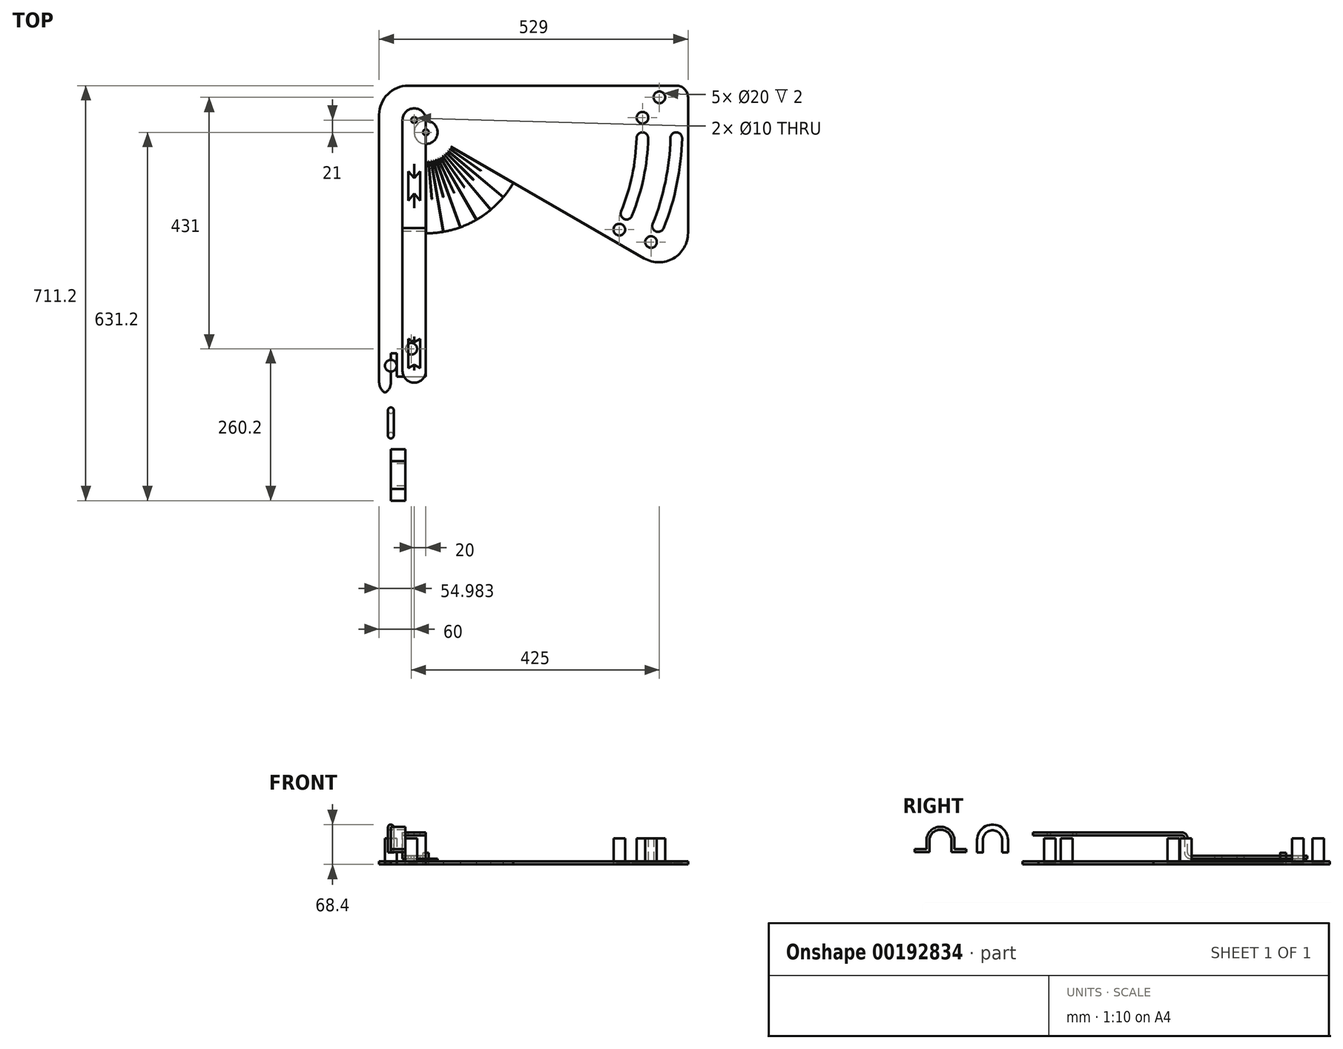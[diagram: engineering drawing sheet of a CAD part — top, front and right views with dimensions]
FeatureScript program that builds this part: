
annotation { "Feature Type Name" : "Feature", "Feature Type Description" : "" }
export const myFeature = defineFeature(function(context is Context, id is Id, definition is map)
    precondition{}
    {
        {
            var Q0;
            Q0=qCreatedBy(makeId("Top.planeOp"),FACE);
            var sketch = newSketch(context, id + "F0", { "sketchPlane" : qUnion([Q0])});
            skLineSegment(sketch, "E0.bottom", {"start": v(0, 0) * mm, "end": v(489, 0) * mm});
            skLineSegment(sketch, "E0.left", {"start": v(0, 0) * mm, "end": v(0, 500) * mm});
            skLineSegment(sketch, "E0.right", {"start": v(489, 0) * mm, "end": v(489, 479) * mm});
            skLineSegment(sketch, "E1.top", {"start": v(0, 0) * mm, "end": v(10, 0) * mm});
            skLineSegment(sketch, "E1.left", {"start": v(0, 489) * mm, "end": v(0, 0) * mm});
            skLineSegment(sketch, "E1.right", {"start": v(10, 50) * mm, "end": v(10, 10) * mm});
            skPoint(sketch, "E2", {"position": v(60, 429) * mm});
            skLineSegment(sketch, "E3", {"start": v(60, 255.9) * mm, "end": v(60, 0) * mm});
            skLineSegment(sketch, "E4", {"start": v(209.9, 342.45) * mm, "end": v(489, 181.32) * mm});
            skLineSegment(sketch, "E5.bottom", {"start": v(10, 48) * mm, "end": v(60, 48) * mm, "construction": true});
            skLineSegment(sketch, "E5.right", {"start": v(60, 48) * mm, "end": v(60, 10) * mm, "construction": true});
            skLineSegment(sketch, "E6.top", {"start": v(441, 429) * mm, "end": v(479, 429) * mm, "construction": true});
            skLineSegment(sketch, "E6.left", {"start": v(441, 479) * mm, "end": v(441, 429) * mm, "construction": true});
            skArc(sketch, "E7", {"start": v(60, 29) * mm, "mid": v(342.84, 146.16) * mm, "end": v(460, 429) * mm, "construction": true});
            skPoint(sketch, "E8", {"position": v(10, 29) * mm});
            skPoint(sketch, "E9", {"position": v(460, 479) * mm});
            skArc(sketch, "E10.0", {"start": v(60, 10) * mm, "mid": v(356.28, 132.72) * mm, "end": v(479, 429) * mm, "construction": true});
            skArc(sketch, "E11.0", {"start": v(60, 48) * mm, "mid": v(329.4, 159.6) * mm, "end": v(441, 429) * mm, "construction": true});
            skLineSegment(sketch, "E12", {"start": v(60, 255.9) * mm, "end": v(209.9, 342.45) * mm, "construction": true});
            skPoint(sketch, "E13.end.orphan", {"position": v(189.9, 354) * mm});
            skPoint(sketch, "E13.start.orphan", {"position": v(60, 279) * mm});
            skCircle(sketch, "E14", {"center": v(60, 429) * mm, "radius": 5 * mm});
            skLineSegment(sketch, "E15.top", {"start": v(489, 489) * mm, "end": v(0, 489) * mm});
            skLineSegment(sketch, "E15.left", {"start": v(489, 479) * mm, "end": v(489, 489) * mm});
            skLineSegment(sketch, "E16", {"start": v(439, 489) * mm, "end": v(439, 479) * mm});
            skLineSegment(sketch, "E17", {"start": v(439, 479) * mm, "end": v(479, 479) * mm});
            skLineSegment(sketch, "E18", {"start": v(479, 479) * mm, "end": v(479, 429) * mm});
            skLineSegment(sketch, "E19", {"start": v(489, 429) * mm, "end": v(479, 429) * mm});
            skArc(sketch, "E20", {"start": v(60, 255.9) * mm, "mid": v(146.55, 279.1) * mm, "end": v(209.9, 342.45) * mm});
            skLineSegment(sketch, "E21", {"start": v(0, 50) * mm, "end": v(10, 50) * mm});
            skLineSegment(sketch, "E22", {"start": v(10, 10) * mm, "end": v(60, 10) * mm});
            skLineSegment(sketch, "E23", {"start": v(60, 0) * mm, "end": v(60, -20) * mm});
            skLineSegment(sketch, "E24", {"start": v(60, -20) * mm, "end": v(0, -20) * mm});
            skLineSegment(sketch, "E25", {"start": v(0, -20) * mm, "end": v(0, 0) * mm});
            skLineSegment(sketch, "E26", {"start": v(0, 489) * mm, "end": v(-20, 489) * mm});
            skLineSegment(sketch, "E27", {"start": v(-20, 489) * mm, "end": v(-20, -20) * mm});
            skLineSegment(sketch, "E28", {"start": v(-20, -20) * mm, "end": v(0, -20) * mm});
            skLineSegment(sketch, "E29", {"start": v(489, 181.32) * mm, "end": v(509, 169.77) * mm});
            skLineSegment(sketch, "E30", {"start": v(509, 169.77) * mm, "end": v(509, 489) * mm});
            skLineSegment(sketch, "E31", {"start": v(509, 489) * mm, "end": v(489, 489) * mm});
            skLineSegment(sketch, "E32", {"start": v(509, 489) * mm, "end": v(509, 509) * mm});
            skLineSegment(sketch, "E33", {"start": v(509, 509) * mm, "end": v(-20, 509) * mm});
            skLineSegment(sketch, "E34", {"start": v(-20, 509) * mm, "end": v(-20, 489) * mm});
            skSolve(sketch);
        }
        {
            var Q0;
            {var subQ3=sQuery(id+"F0.wireOp",EDGE,"E1.right");Q0=makeQuery(id+"F0.imprint","IMPRINT",FACE,{"disambiguationData":[TD([[makeQuery(id+"F0.imprint","IMPRINT",EDGE,{"derivedFrom":subQ3}),1.0]])]});}
            var Q1;
            {var subQ2=sQuery(id+"F0.wireOp",EDGE,"E1.top");Q1=makeQuery(id+"F0.imprint","IMPRINT",FACE,{"disambiguationData":[TD([[makeQuery(id+"F0.imprint","IMPRINT",EDGE,{"derivedFrom":subQ2}),1.0]])]});}
            var Q2;
            {var subQ1=sQuery(id+"F0.wireOp",EDGE,"E15.left");Q2=makeQuery(id+"F0.imprint","IMPRINT",FACE,{"disambiguationData":[TD([[makeQuery(id+"F0.imprint","IMPRINT",EDGE,{"derivedFrom":subQ1}),1.0]])]});}
            var Q3;
            {var subQ1=sQuery(id+"F0.wireOp",EDGE,"E25");Q3=makeQuery(id+"F0.imprint","IMPRINT",FACE,{"disambiguationData":[TD([[makeQuery(id+"F0.imprint","IMPRINT",EDGE,{"derivedFrom":subQ1}),1.0]])]});}
            var Q4;
            {var subQ0=sQuery(id+"F0.wireOp",EDGE,"E1.top");Q4=makeQuery(id+"F0.imprint","IMPRINT",FACE,{"disambiguationData":[TD([[makeQuery(id+"F0.imprint","IMPRINT",EDGE,{"derivedFrom":subQ0}),-1.0]])]});}
            var Q5;
            {var subQ3=sQuery(id+"F0.wireOp",EDGE,"E26");Q5=makeQuery(id+"F0.imprint","IMPRINT",FACE,{"disambiguationData":[TD([[makeQuery(id+"F0.imprint","IMPRINT",EDGE,{"derivedFrom":subQ3}),-1.0]])]});}
            var Q6;
            {var subQ1=sQuery(id+"F0.wireOp",EDGE,"E15.left");Q6=makeQuery(id+"F0.imprint","IMPRINT",FACE,{"disambiguationData":[TD([[makeQuery(id+"F0.imprint","IMPRINT",EDGE,{"derivedFrom":subQ1}),-1.0]])]});}
            extrude(context, id + "F1", {"entities" : qUnion([Q0, Q1, Q2, Q3, Q4, Q5, Q6]), "depth" : 5 * mm});
        }
        {
            var Q0;
            Q0=makeQuery(id+"F1.opExtrude","SWEPT_FACE",FACE,{"disambiguationData":[OSD([sQuery(id+"F0.wireOp",EDGE,"E33")])]});
            cPlane(context, id + "F2", {"entities" : qUnion([Q0]), "cplaneType" : CPlaneType.OFFSET, "offset" : 80 * mm, "oppositeDirection" : true, "width" : 150 * mm, "height" : 150 * mm});
        }
        {
            var Q0;
            Q0=qCreatedBy(id+"F2.planeOp",FACE);
            var sketch = newSketch(context, id + "F3", { "sketchPlane" : qUnion([Q0])});
            skLineSegment(sketch, "E35", {"start": v(-60, 20) * mm, "end": v(-60, 0) * mm});
            skLineSegment(sketch, "E36", {"start": v(-60, 20) * mm, "end": v(-65, 20) * mm});
            skLineSegment(sketch, "E37", {"start": v(-65, 20) * mm, "end": v(-65, 10) * mm});
            skLineSegment(sketch, "E38", {"start": v(-65, 10) * mm, "end": v(-80, 10) * mm});
            skLineSegment(sketch, "E39", {"start": v(-80, 10) * mm, "end": v(-80, 5) * mm});
            skLineSegment(sketch, "E40", {"start": v(-80, 5) * mm, "end": v(-65, 5) * mm});
            skLineSegment(sketch, "E41", {"start": v(-65, 5) * mm, "end": v(-65, 0) * mm});
            skLineSegment(sketch, "E42", {"start": v(-65, 0) * mm, "end": v(-60, 0) * mm});
            skSolve(sketch);
        }
        {
            var Q0;
            Q0=qSketchRegion(id+"F3",true);
            var Q1;
            Q1=sQuery(id+"F3.wireOp",EDGE,"E35");
            revolve(context, id + "F4", {"entities" : qUnion([Q0]), "axis" : qUnion([Q1]), "revolveType" : RevolveType.FULL});
        }
        {
            var Q0;
            Q0=makeQuery(id+"F1.opExtrude","CAP_FACE",FACE,{"disambiguationData":[OSD([sQuery(id+"F0.wireOp",EDGE,"E0.bottom"),sQuery(id+"F0.wireOp",EDGE,"E0.top"),sQuery(id+"F0.wireOp",EDGE,"E0.right"),sQuery(id+"F0.wireOp",EDGE,"E1.right"),sQuery(id+"F0.wireOp",EDGE,"E3"),sQuery(id+"F0.wireOp",EDGE,"E4"),sQuery(id+"F0.wireOp",EDGE,"E12"),sQuery(id+"F0.wireOp",EDGE,"E14")])],"isStart":false});
            cPlane(context, id + "F5", {"entities" : qUnion([Q0]), "cplaneType" : CPlaneType.OFFSET, "offset" : 0 * mm, "width" : 150 * mm, "height" : 150 * mm});
        }
        {
            var Q0;
            Q0=qCreatedBy(id+"F5.planeOp",FACE);
            var sketch = newSketch(context, id + "F6", { "sketchPlane" : qUnion([Q0])});
            skCircle(sketch, "E43", {"center": v(34.98, 58) * mm, "radius": 10 * mm});
            skLineSegment(sketch, "E44.bottom", {"start": v(9.98, 10) * mm, "end": v(59.98, 10) * mm, "construction": true});
            skLineSegment(sketch, "E44.top", {"start": v(9.98, 48) * mm, "end": v(59.98, 48) * mm, "construction": true});
            skLineSegment(sketch, "E44.left", {"start": v(9.98, 10) * mm, "end": v(9.98, 48) * mm, "construction": true});
            skLineSegment(sketch, "E44.right", {"start": v(59.98, 10) * mm, "end": v(59.98, 48) * mm, "construction": true});
            skLineSegment(sketch, "E45.bottom", {"start": v(478.98, 479) * mm, "end": v(440.98, 479) * mm, "construction": true});
            skLineSegment(sketch, "E45.top", {"start": v(478.98, 429) * mm, "end": v(440.98, 429) * mm, "construction": true});
            skLineSegment(sketch, "E45.left", {"start": v(478.98, 479) * mm, "end": v(478.98, 429) * mm, "construction": true});
            skLineSegment(sketch, "E45.right", {"start": v(440.98, 479) * mm, "end": v(440.98, 429) * mm, "construction": true});
            skArc(sketch, "E46", {"start": v(59.98, 29) * mm, "mid": v(342.83, 146.16) * mm, "end": v(459.98, 429) * mm, "construction": true});
            skArc(sketch, "E47.0", {"start": v(59.98, 10) * mm, "mid": v(356.26, 132.72) * mm, "end": v(478.98, 429) * mm, "construction": true});
            skArc(sketch, "E48.0", {"start": v(59.98, 48) * mm, "mid": v(329.4, 159.6) * mm, "end": v(440.98, 429) * mm, "construction": true});
            skLineSegment(sketch, "E49", {"start": v(459.98, 429) * mm, "end": v(459.98, 479) * mm, "construction": true});
            skLineSegment(sketch, "E50", {"start": v(59.98, 29) * mm, "end": v(9.98, 29) * mm, "construction": true});
            skCircle(sketch, "E51", {"center": v(430.98, 454) * mm, "radius": 10 * mm});
            skCircle(sketch, "E52", {"center": v(445.6, 241.01) * mm, "radius": 10 * mm});
            skLineSegment(sketch, "E53", {"start": v(445.6, 241.01) * mm, "end": v(391.37, 262.2) * mm, "construction": true});
            skCircle(sketch, "E54", {"center": v(391.37, 262.2) * mm, "radius": 10 * mm});
            skCircle(sketch, "E55.MirrorC", {"center": v(34.98, 0) * mm, "radius": 10 * mm});
            skCircle(sketch, "E56", {"center": v(-0.02, 29) * mm, "radius": 10 * mm});
            skLineSegment(sketch, "E57", {"start": v(34.98, 0) * mm, "end": v(34.98, 48) * mm, "construction": true});
            skCircle(sketch, "E58.MirrorC", {"center": v(488.98, 454) * mm, "radius": 10 * mm});
            skLineSegment(sketch, "E59", {"start": v(430.98, 454) * mm, "end": v(488.98, 454) * mm, "construction": true});
            skCircle(sketch, "E60", {"center": v(459.98, 489) * mm, "radius": 10 * mm});
            skSolve(sketch);
        }
        {
            var Q0;
            Q0=makeQuery(id+"F6.imprint","IMPRINT",FACE,{"disambiguationData":[TD([[makeQuery(id+"F6.imprint","IMPRINT",EDGE,{"derivedFrom":sQuery(id+"F6.wireOp",EDGE,"E58.MirrorC")}),-1.0]])]});
            var Q1;
            Q1=makeQuery(id+"F6.imprint","IMPRINT",FACE,{"disambiguationData":[TD([[makeQuery(id+"F6.imprint","IMPRINT",EDGE,{"derivedFrom":sQuery(id+"F6.wireOp",EDGE,"E60")}),1.0]])]});
            var Q2;
            Q2=makeQuery(id+"F6.imprint","IMPRINT",FACE,{"disambiguationData":[TD([[makeQuery(id+"F6.imprint","IMPRINT",EDGE,{"derivedFrom":sQuery(id+"F6.wireOp",EDGE,"E51")}),1.0]])]});
            var Q3;
            Q3=makeQuery(id+"F6.imprint","IMPRINT",FACE,{"disambiguationData":[TD([[makeQuery(id+"F6.imprint","IMPRINT",EDGE,{"derivedFrom":sQuery(id+"F6.wireOp",EDGE,"E52")}),1.0]])]});
            var Q4;
            Q4=makeQuery(id+"F6.imprint","IMPRINT",FACE,{"disambiguationData":[TD([[makeQuery(id+"F6.imprint","IMPRINT",EDGE,{"derivedFrom":sQuery(id+"F6.wireOp",EDGE,"E54")}),1.0]])]});
            var Q5;
            Q5=makeQuery(id+"F6.imprint","IMPRINT",FACE,{"disambiguationData":[TD([[makeQuery(id+"F6.imprint","IMPRINT",EDGE,{"derivedFrom":sQuery(id+"F6.wireOp",EDGE,"E55.MirrorC")}),-1.0]])]});
            var Q6;
            Q6=makeQuery(id+"F6.imprint","IMPRINT",FACE,{"disambiguationData":[TD([[makeQuery(id+"F6.imprint","IMPRINT",EDGE,{"derivedFrom":sQuery(id+"F6.wireOp",EDGE,"E43")}),1.0]])]});
            var Q7;
            Q7=makeQuery(id+"F6.imprint","IMPRINT",FACE,{"disambiguationData":[TD([[makeQuery(id+"F6.imprint","IMPRINT",EDGE,{"derivedFrom":sQuery(id+"F6.wireOp",EDGE,"E56")}),1.0]])]});
            extrude(context, id + "F7", {"entities" : qUnion([Q0, Q1, Q2, Q3, Q4, Q5, Q6, Q7]), "operationType" : NewBodyOperationType.REMOVE, "oppositeDirection" : true, "depth" : 2 * mm});
        }
        {
            var Q0;
            Q0=makeQuery(id+"F6.imprint","IMPRINT",FACE,{"disambiguationData":[TD([[makeQuery(id+"F6.imprint","IMPRINT",EDGE,{"derivedFrom":sQuery(id+"F6.wireOp",EDGE,"E58.MirrorC")}),-1.0]])]});
            var Q1;
            Q1=makeQuery(id+"F6.imprint","IMPRINT",FACE,{"disambiguationData":[TD([[makeQuery(id+"F6.imprint","IMPRINT",EDGE,{"derivedFrom":sQuery(id+"F6.wireOp",EDGE,"E60")}),1.0]])]});
            var Q2;
            Q2=makeQuery(id+"F6.imprint","IMPRINT",FACE,{"disambiguationData":[TD([[makeQuery(id+"F6.imprint","IMPRINT",EDGE,{"derivedFrom":sQuery(id+"F6.wireOp",EDGE,"E51")}),1.0]])]});
            var Q3;
            Q3=makeQuery(id+"F6.imprint","IMPRINT",FACE,{"disambiguationData":[TD([[makeQuery(id+"F6.imprint","IMPRINT",EDGE,{"derivedFrom":sQuery(id+"F6.wireOp",EDGE,"E52")}),1.0]])]});
            var Q4;
            Q4=makeQuery(id+"F6.imprint","IMPRINT",FACE,{"disambiguationData":[TD([[makeQuery(id+"F6.imprint","IMPRINT",EDGE,{"derivedFrom":sQuery(id+"F6.wireOp",EDGE,"E54")}),1.0]])]});
            var Q5;
            Q5=makeQuery(id+"F6.imprint","IMPRINT",FACE,{"disambiguationData":[TD([[makeQuery(id+"F6.imprint","IMPRINT",EDGE,{"derivedFrom":sQuery(id+"F6.wireOp",EDGE,"E56")}),1.0]])]});
            var Q6;
            Q6=makeQuery(id+"F6.imprint","IMPRINT",FACE,{"disambiguationData":[TD([[makeQuery(id+"F6.imprint","IMPRINT",EDGE,{"derivedFrom":sQuery(id+"F6.wireOp",EDGE,"E55.MirrorC")}),-1.0]])]});
            var Q7;
            Q7=makeQuery(id+"F6.imprint","IMPRINT",FACE,{"disambiguationData":[TD([[makeQuery(id+"F6.imprint","IMPRINT",EDGE,{"derivedFrom":sQuery(id+"F6.wireOp",EDGE,"E43")}),1.0]])]});
            extrude(context, id + "F8", {"entities" : qUnion([Q0, Q1, Q2, Q3, Q4, Q5, Q6, Q7]), "depth" : 40 * mm});
        }
        {
            var Q0;
            Q0=makeQuery(id+"F1.opExtrude","CAP_FACE",FACE,{"disambiguationData":[OSD([sQuery(id+"F0.wireOp",EDGE,"E0.bottom"),sQuery(id+"F0.wireOp",EDGE,"E0.right"),sQuery(id+"F0.wireOp",EDGE,"E1.right"),sQuery(id+"F0.wireOp",EDGE,"E3"),sQuery(id+"F0.wireOp",EDGE,"E4"),sQuery(id+"F0.wireOp",EDGE,"E12"),sQuery(id+"F0.wireOp",EDGE,"E14"),sQuery(id+"F0.wireOp",EDGE,"E15.top"),sQuery(id+"F0.wireOp",EDGE,"E16"),sQuery(id+"F0.wireOp",EDGE,"E17"),sQuery(id+"F0.wireOp",EDGE,"E18"),sQuery(id+"F0.wireOp",EDGE,"E19")])],"isStart":false});
            var sketch = newSketch(context, id + "F9", { "sketchPlane" : qUnion([Q0])});
            skLineSegment(sketch, "E61", {"start": v(60, 379) * mm, "end": v(60, 255.9) * mm});
            skLineSegment(sketch, "E62", {"start": v(103.3, 404) * mm, "end": v(209.9, 342.45) * mm});
            skArc(sketch, "E63", {"start": v(60, 314) * mm, "mid": v(117.5, 329.4) * mm, "end": v(159.6, 371.5) * mm});
            skLineSegment(sketch, "E64.0", {"start": v(64.45, 426.72) * mm, "end": v(210.03, 342.67) * mm});
            skArc(sketch, "E65", {"start": v(60, 424) * mm, "mid": v(62.6, 424.73) * mm, "end": v(64.45, 426.72) * mm});
            skLineSegment(sketch, "E66.trimOffspring", {"start": v(64.2, 426.29) * mm, "end": v(64.83, 425.92) * mm});
            skLineSegment(sketch, "E67", {"start": v(210.03, 342.67) * mm, "end": v(209.9, 342.45) * mm});
            skLineSegment(sketch, "E68", {"start": v(100.96, 400.32) * mm, "end": v(154.2, 363.04) * mm});
            skLineSegment(sketch, "E69", {"start": v(98.3, 396.86) * mm, "end": v(192.6, 317.74) * mm});
            skLineSegment(sketch, "E70", {"start": v(95.36, 393.64) * mm, "end": v(141.32, 347.68) * mm});
            skLineSegment(sketch, "E71", {"start": v(92.14, 390.7) * mm, "end": v(171.26, 296.4) * mm});
            skLineSegment(sketch, "E72", {"start": v(88.68, 388.04) * mm, "end": v(125.96, 334.8) * mm});
            skLineSegment(sketch, "E73", {"start": v(85, 385.7) * mm, "end": v(146.55, 279.1) * mm});
            skLineSegment(sketch, "E74", {"start": v(81.13, 383.68) * mm, "end": v(108.6, 324.77) * mm});
            skLineSegment(sketch, "E75", {"start": v(77.1, 382.02) * mm, "end": v(119.2, 266.34) * mm});
            skLineSegment(sketch, "E76", {"start": v(72.94, 380.7) * mm, "end": v(89.76, 317.92) * mm});
            skLineSegment(sketch, "E77", {"start": v(68.68, 379.76) * mm, "end": v(90.06, 258.54) * mm});
            skLineSegment(sketch, "E78", {"start": v(64.36, 379.2) * mm, "end": v(70.02, 314.44) * mm});
            skArc(sketch, "E79", {"start": v(60, 255.9) * mm, "mid": v(146.55, 279.1) * mm, "end": v(209.9, 342.45) * mm, "construction": true});
            skPoint(sketch, "E80.orphan", {"position": v(117.5, 329.4) * mm});
            skLineSegment(sketch, "E81.0", {"start": v(64.24, 426.34) * mm, "end": v(64.83, 425.92) * mm});
            skLineSegment(sketch, "E82.0", {"start": v(63.95, 425.93) * mm, "end": v(64.55, 425.51) * mm});
            skLineSegment(sketch, "E83.0", {"start": v(63.67, 425.6) * mm, "end": v(64.23, 425.13) * mm});
            skLineSegment(sketch, "E84.0", {"start": v(64, 425.98) * mm, "end": v(64.55, 425.51) * mm});
            skLineSegment(sketch, "E85.0", {"start": v(63.36, 425.29) * mm, "end": v(63.87, 424.77) * mm});
            skLineSegment(sketch, "E86.0", {"start": v(63.71, 425.64) * mm, "end": v(64.23, 425.13) * mm});
            skLineSegment(sketch, "E87.0", {"start": v(63.02, 425) * mm, "end": v(63.49, 424.45) * mm});
            skLineSegment(sketch, "E88.0", {"start": v(63.4, 425.33) * mm, "end": v(63.87, 424.77) * mm});
            skLineSegment(sketch, "E89.0", {"start": v(63.07, 425.05) * mm, "end": v(63.49, 424.45) * mm});
            skLineSegment(sketch, "E90.0", {"start": v(62.66, 424.76) * mm, "end": v(63.08, 424.17) * mm});
            skLineSegment(sketch, "E91.0", {"start": v(55.7, 435.96) * mm, "end": v(62.65, 423.92) * mm});
            skLineSegment(sketch, "E92.0", {"start": v(56.12, 436.21) * mm, "end": v(63.08, 424.17) * mm});
            skLineSegment(sketch, "E93.0", {"start": v(61.89, 424.36) * mm, "end": v(62.2, 423.7) * mm});
            skLineSegment(sketch, "E94.0", {"start": v(62.34, 424.57) * mm, "end": v(62.65, 423.92) * mm});
            skLineSegment(sketch, "E95.0", {"start": v(61.48, 424.22) * mm, "end": v(61.72, 423.53) * mm});
            skLineSegment(sketch, "E96.0", {"start": v(61.95, 424.39) * mm, "end": v(62.2, 423.7) * mm});
            skLineSegment(sketch, "E97.0", {"start": v(61.05, 424.1) * mm, "end": v(61.24, 423.4) * mm});
            skLineSegment(sketch, "E98.0", {"start": v(61.54, 424.24) * mm, "end": v(61.72, 423.53) * mm});
            skLineSegment(sketch, "E99.0", {"start": v(60.62, 424.03) * mm, "end": v(60.75, 423.32) * mm});
            skLineSegment(sketch, "E100.0", {"start": v(61.11, 424.12) * mm, "end": v(61.24, 423.4) * mm});
            skLineSegment(sketch, "E101.0", {"start": v(60.19, 424) * mm, "end": v(60.25, 423.27) * mm});
            skLineSegment(sketch, "E102.0", {"start": v(60.68, 424.04) * mm, "end": v(60.75, 423.32) * mm});
            skLineSegment(sketch, "E103.0", {"start": v(59.75, 429) * mm, "end": v(59.75, 255.9) * mm});
            skLineSegment(sketch, "E104.0", {"start": v(60.25, 424) * mm, "end": v(60.25, 423.27) * mm});
            skArc(sketch, "E105", {"start": v(103.3, 404) * mm, "mid": v(85, 385.7) * mm, "end": v(60, 379) * mm});
            skLineSegment(sketch, "E106.trimOffspring", {"start": v(60.25, 379) * mm, "end": v(60.25, 255.9) * mm});
            skLineSegment(sketch, "E107.trimOffspring", {"start": v(64.1, 379.17) * mm, "end": v(69.77, 314.42) * mm});
            skLineSegment(sketch, "E108.trimOffspring", {"start": v(64.6, 379.21) * mm, "end": v(70.27, 314.46) * mm});
            skLineSegment(sketch, "E109.trimOffspring", {"start": v(68.44, 379.72) * mm, "end": v(89.81, 258.5) * mm});
            skLineSegment(sketch, "E110.trimOffspring", {"start": v(68.93, 379.8) * mm, "end": v(90.3, 258.58) * mm});
            skLineSegment(sketch, "E111.trimOffspring", {"start": v(72.7, 380.64) * mm, "end": v(89.52, 317.85) * mm});
            skLineSegment(sketch, "E112.trimOffspring", {"start": v(73.18, 380.77) * mm, "end": v(90, 317.98) * mm});
            skLineSegment(sketch, "E113.trimOffspring", {"start": v(76.87, 381.93) * mm, "end": v(118.97, 266.26) * mm});
            skLineSegment(sketch, "E114.trimOffspring", {"start": v(77.34, 382.1) * mm, "end": v(119.44, 266.43) * mm});
            skLineSegment(sketch, "E115.trimOffspring", {"start": v(80.9, 383.58) * mm, "end": v(108.37, 324.67) * mm});
            skLineSegment(sketch, "E116.trimOffspring", {"start": v(81.36, 383.8) * mm, "end": v(108.83, 324.88) * mm});
            skLineSegment(sketch, "E117.trimOffspring", {"start": v(88.47, 387.9) * mm, "end": v(125.76, 334.65) * mm});
            skLineSegment(sketch, "E118.trimOffspring", {"start": v(88.88, 388.19) * mm, "end": v(126.17, 334.94) * mm});
            skLineSegment(sketch, "E119.trimOffspring", {"start": v(84.78, 385.57) * mm, "end": v(146.33, 278.97) * mm});
            skLineSegment(sketch, "E120.trimOffspring", {"start": v(85.22, 385.82) * mm, "end": v(146.76, 279.22) * mm});
            skLineSegment(sketch, "E121.trimOffspring", {"start": v(91.95, 390.54) * mm, "end": v(171.07, 296.24) * mm});
            skLineSegment(sketch, "E122.trimOffspring", {"start": v(92.33, 390.86) * mm, "end": v(171.45, 296.56) * mm});
            skLineSegment(sketch, "E123.trimOffspring", {"start": v(95.18, 393.47) * mm, "end": v(141.14, 347.5) * mm});
            skLineSegment(sketch, "E124.trimOffspring", {"start": v(95.53, 393.82) * mm, "end": v(141.5, 347.86) * mm});
            skLineSegment(sketch, "E125.trimOffspring", {"start": v(98.14, 396.67) * mm, "end": v(192.44, 317.55) * mm});
            skLineSegment(sketch, "E126.trimOffspring", {"start": v(98.46, 397.05) * mm, "end": v(192.76, 317.93) * mm});
            skLineSegment(sketch, "E127.trimOffspring", {"start": v(100.81, 400.12) * mm, "end": v(154.06, 362.83) * mm});
            skLineSegment(sketch, "E128.trimOffspring", {"start": v(101.1, 400.53) * mm, "end": v(154.35, 363.24) * mm});
            skLineSegment(sketch, "E129.trimOffspring", {"start": v(103.18, 403.78) * mm, "end": v(209.78, 342.24) * mm});
            skArc(sketch, "E130", {"start": v(209.9, 342.45) * mm, "mid": v(146.55, 279.1) * mm, "end": v(60, 255.9) * mm});
            skSolve(sketch);
        }
        {
            var Q0;
            {var subQ0=sQuery(id+"F9.wireOp",EDGE,"E105");var subQ1=sQuery(id+"F9.wireOp",EDGE,"E62");var subQ2=makeQuery(id+"F9.imprint","INTERSECT",VERTEX,{"derivedFrom":[subQ1,subQ0]});Q0=makeQuery(id+"F9.imprint","IMPRINT",FACE,{"disambiguationData":[TD([[makeQuery(id+"F9.imprint","IMPRINT",EDGE,{"disambiguationData":[TD([[subQ2,-1.0]])],"derivedFrom":subQ1}),-1.0]])]});}
            var Q1;
            {var subQ0=sQuery(id+"F9.wireOp",EDGE,"E62");var subQ3=sQuery(id+"F9.wireOp",EDGE,"E63");var subQ4=makeQuery(id+"F9.imprint","INTERSECT",VERTEX,{"derivedFrom":[subQ0,subQ3]});Q1=makeQuery(id+"F9.imprint","IMPRINT",FACE,{"disambiguationData":[TD([[makeQuery(id+"F9.imprint","IMPRINT",EDGE,{"disambiguationData":[TD([[subQ4,1.0]])],"derivedFrom":subQ3}),-1.0]])]});}
            var Q2;
            {var subQ0=sQuery(id+"F9.wireOp",EDGE,"E68");Q2=makeQuery(id+"F9.imprint","IMPRINT",FACE,{"disambiguationData":[TD([[makeQuery(id+"F9.imprint","IMPRINT",EDGE,{"derivedFrom":subQ0}),1.0]])]});}
            var Q3;
            {var subQ0=sQuery(id+"F9.wireOp",EDGE,"E68");Q3=makeQuery(id+"F9.imprint","IMPRINT",FACE,{"disambiguationData":[TD([[makeQuery(id+"F9.imprint","IMPRINT",EDGE,{"derivedFrom":subQ0}),-1.0]])]});}
            var Q4;
            {var subQ0=sQuery(id+"F9.wireOp",EDGE,"E69");var subQ1=sQuery(id+"F9.wireOp",EDGE,"E63");var subQ2=makeQuery(id+"F9.imprint","INTERSECT",VERTEX,{"derivedFrom":[subQ1,subQ0]});Q4=makeQuery(id+"F9.imprint","IMPRINT",FACE,{"disambiguationData":[TD([[makeQuery(id+"F9.imprint","IMPRINT",EDGE,{"disambiguationData":[TD([[subQ2,-1.0]])],"derivedFrom":subQ1}),1.0]])]});}
            var Q5;
            {var subQ0=sQuery(id+"F9.wireOp",EDGE,"E125.trimOffspring");var subQ1=sQuery(id+"F9.wireOp",EDGE,"E63");var subQ2=makeQuery(id+"F9.imprint","INTERSECT",VERTEX,{"derivedFrom":[subQ1,subQ0]});Q5=makeQuery(id+"F9.imprint","IMPRINT",FACE,{"disambiguationData":[TD([[makeQuery(id+"F9.imprint","IMPRINT",EDGE,{"disambiguationData":[TD([[subQ2,-1.0]])],"derivedFrom":subQ1}),1.0]])]});}
            var Q6;
            {var subQ0=sQuery(id+"F9.wireOp",EDGE,"E125.trimOffspring");var subQ1=sQuery(id+"F9.wireOp",EDGE,"E63");var subQ2=makeQuery(id+"F9.imprint","INTERSECT",VERTEX,{"derivedFrom":[subQ1,subQ0]});Q6=makeQuery(id+"F9.imprint","IMPRINT",FACE,{"disambiguationData":[TD([[makeQuery(id+"F9.imprint","IMPRINT",EDGE,{"disambiguationData":[TD([[subQ2,-1.0]])],"derivedFrom":subQ1}),-1.0]])]});}
            var Q7;
            {var subQ0=sQuery(id+"F9.wireOp",EDGE,"E69");var subQ1=sQuery(id+"F9.wireOp",EDGE,"E63");var subQ2=makeQuery(id+"F9.imprint","INTERSECT",VERTEX,{"derivedFrom":[subQ1,subQ0]});Q7=makeQuery(id+"F9.imprint","IMPRINT",FACE,{"disambiguationData":[TD([[makeQuery(id+"F9.imprint","IMPRINT",EDGE,{"disambiguationData":[TD([[subQ2,-1.0]])],"derivedFrom":subQ1}),-1.0]])]});}
            var Q8;
            {var subQ0=sQuery(id+"F9.wireOp",EDGE,"E70");Q8=makeQuery(id+"F9.imprint","IMPRINT",FACE,{"disambiguationData":[TD([[makeQuery(id+"F9.imprint","IMPRINT",EDGE,{"derivedFrom":subQ0}),-1.0]])]});}
            var Q9;
            {var subQ0=sQuery(id+"F9.wireOp",EDGE,"E70");Q9=makeQuery(id+"F9.imprint","IMPRINT",FACE,{"disambiguationData":[TD([[makeQuery(id+"F9.imprint","IMPRINT",EDGE,{"derivedFrom":subQ0}),1.0]])]});}
            var Q10;
            {var subQ0=sQuery(id+"F9.wireOp",EDGE,"E71");var subQ1=sQuery(id+"F9.wireOp",EDGE,"E63");var subQ2=makeQuery(id+"F9.imprint","INTERSECT",VERTEX,{"derivedFrom":[subQ1,subQ0]});Q10=makeQuery(id+"F9.imprint","IMPRINT",FACE,{"disambiguationData":[TD([[makeQuery(id+"F9.imprint","IMPRINT",EDGE,{"disambiguationData":[TD([[subQ2,-1.0]])],"derivedFrom":subQ1}),1.0]])]});}
            var Q11;
            {var subQ0=sQuery(id+"F9.wireOp",EDGE,"E71");var subQ1=sQuery(id+"F9.wireOp",EDGE,"E63");var subQ2=makeQuery(id+"F9.imprint","INTERSECT",VERTEX,{"derivedFrom":[subQ1,subQ0]});Q11=makeQuery(id+"F9.imprint","IMPRINT",FACE,{"disambiguationData":[TD([[makeQuery(id+"F9.imprint","IMPRINT",EDGE,{"disambiguationData":[TD([[subQ2,-1.0]])],"derivedFrom":subQ1}),-1.0]])]});}
            var Q12;
            {var subQ0=sQuery(id+"F9.wireOp",EDGE,"E121.trimOffspring");var subQ1=sQuery(id+"F9.wireOp",EDGE,"E63");var subQ2=makeQuery(id+"F9.imprint","INTERSECT",VERTEX,{"derivedFrom":[subQ1,subQ0]});Q12=makeQuery(id+"F9.imprint","IMPRINT",FACE,{"disambiguationData":[TD([[makeQuery(id+"F9.imprint","IMPRINT",EDGE,{"disambiguationData":[TD([[subQ2,-1.0]])],"derivedFrom":subQ1}),-1.0]])]});}
            var Q13;
            {var subQ0=sQuery(id+"F9.wireOp",EDGE,"E121.trimOffspring");var subQ1=sQuery(id+"F9.wireOp",EDGE,"E63");var subQ2=makeQuery(id+"F9.imprint","INTERSECT",VERTEX,{"derivedFrom":[subQ1,subQ0]});Q13=makeQuery(id+"F9.imprint","IMPRINT",FACE,{"disambiguationData":[TD([[makeQuery(id+"F9.imprint","IMPRINT",EDGE,{"disambiguationData":[TD([[subQ2,-1.0]])],"derivedFrom":subQ1}),1.0]])]});}
            var Q14;
            {var subQ0=sQuery(id+"F9.wireOp",EDGE,"E72");Q14=makeQuery(id+"F9.imprint","IMPRINT",FACE,{"disambiguationData":[TD([[makeQuery(id+"F9.imprint","IMPRINT",EDGE,{"derivedFrom":subQ0}),1.0]])]});}
            var Q15;
            {var subQ0=sQuery(id+"F9.wireOp",EDGE,"E72");Q15=makeQuery(id+"F9.imprint","IMPRINT",FACE,{"disambiguationData":[TD([[makeQuery(id+"F9.imprint","IMPRINT",EDGE,{"derivedFrom":subQ0}),-1.0]])]});}
            var Q16;
            {var subQ0=sQuery(id+"F9.wireOp",EDGE,"E120.trimOffspring");var subQ1=sQuery(id+"F9.wireOp",EDGE,"E63");var subQ2=makeQuery(id+"F9.imprint","INTERSECT",VERTEX,{"derivedFrom":[subQ1,subQ0]});Q16=makeQuery(id+"F9.imprint","IMPRINT",FACE,{"disambiguationData":[TD([[makeQuery(id+"F9.imprint","IMPRINT",EDGE,{"disambiguationData":[TD([[subQ2,1.0]])],"derivedFrom":subQ1}),1.0]])]});}
            var Q17;
            {var subQ0=sQuery(id+"F9.wireOp",EDGE,"E119.trimOffspring");var subQ1=sQuery(id+"F9.wireOp",EDGE,"E63");var subQ2=makeQuery(id+"F9.imprint","INTERSECT",VERTEX,{"derivedFrom":[subQ1,subQ0]});Q17=makeQuery(id+"F9.imprint","IMPRINT",FACE,{"disambiguationData":[TD([[makeQuery(id+"F9.imprint","IMPRINT",EDGE,{"disambiguationData":[TD([[subQ2,-1.0]])],"derivedFrom":subQ1}),1.0]])]});}
            var Q18;
            {var subQ0=sQuery(id+"F9.wireOp",EDGE,"E74");Q18=makeQuery(id+"F9.imprint","IMPRINT",FACE,{"disambiguationData":[TD([[makeQuery(id+"F9.imprint","IMPRINT",EDGE,{"derivedFrom":subQ0}),-1.0]])]});}
            var Q19;
            {var subQ0=sQuery(id+"F9.wireOp",EDGE,"E74");Q19=makeQuery(id+"F9.imprint","IMPRINT",FACE,{"disambiguationData":[TD([[makeQuery(id+"F9.imprint","IMPRINT",EDGE,{"derivedFrom":subQ0}),1.0]])]});}
            var Q20;
            {var subQ0=sQuery(id+"F9.wireOp",EDGE,"E75");var subQ1=sQuery(id+"F9.wireOp",EDGE,"E63");var subQ2=makeQuery(id+"F9.imprint","INTERSECT",VERTEX,{"derivedFrom":[subQ1,subQ0]});Q20=makeQuery(id+"F9.imprint","IMPRINT",FACE,{"disambiguationData":[TD([[makeQuery(id+"F9.imprint","IMPRINT",EDGE,{"disambiguationData":[TD([[subQ2,-1.0]])],"derivedFrom":subQ1}),1.0]])]});}
            var Q21;
            {var subQ0=sQuery(id+"F9.wireOp",EDGE,"E113.trimOffspring");var subQ1=sQuery(id+"F9.wireOp",EDGE,"E63");var subQ2=makeQuery(id+"F9.imprint","INTERSECT",VERTEX,{"derivedFrom":[subQ1,subQ0]});Q21=makeQuery(id+"F9.imprint","IMPRINT",FACE,{"disambiguationData":[TD([[makeQuery(id+"F9.imprint","IMPRINT",EDGE,{"disambiguationData":[TD([[subQ2,-1.0]])],"derivedFrom":subQ1}),1.0]])]});}
            var Q22;
            {var subQ0=sQuery(id+"F9.wireOp",EDGE,"E113.trimOffspring");var subQ1=sQuery(id+"F9.wireOp",EDGE,"E63");var subQ2=makeQuery(id+"F9.imprint","INTERSECT",VERTEX,{"derivedFrom":[subQ1,subQ0]});Q22=makeQuery(id+"F9.imprint","IMPRINT",FACE,{"disambiguationData":[TD([[makeQuery(id+"F9.imprint","IMPRINT",EDGE,{"disambiguationData":[TD([[subQ2,-1.0]])],"derivedFrom":subQ1}),-1.0]])]});}
            var Q23;
            {var subQ0=sQuery(id+"F9.wireOp",EDGE,"E75");var subQ1=sQuery(id+"F9.wireOp",EDGE,"E63");var subQ2=makeQuery(id+"F9.imprint","INTERSECT",VERTEX,{"derivedFrom":[subQ1,subQ0]});Q23=makeQuery(id+"F9.imprint","IMPRINT",FACE,{"disambiguationData":[TD([[makeQuery(id+"F9.imprint","IMPRINT",EDGE,{"disambiguationData":[TD([[subQ2,-1.0]])],"derivedFrom":subQ1}),-1.0]])]});}
            var Q24;
            {var subQ0=sQuery(id+"F9.wireOp",EDGE,"E76");Q24=makeQuery(id+"F9.imprint","IMPRINT",FACE,{"disambiguationData":[TD([[makeQuery(id+"F9.imprint","IMPRINT",EDGE,{"derivedFrom":subQ0}),1.0]])]});}
            var Q25;
            {var subQ0=sQuery(id+"F9.wireOp",EDGE,"E76");Q25=makeQuery(id+"F9.imprint","IMPRINT",FACE,{"disambiguationData":[TD([[makeQuery(id+"F9.imprint","IMPRINT",EDGE,{"derivedFrom":subQ0}),-1.0]])]});}
            var Q26;
            {var subQ0=sQuery(id+"F9.wireOp",EDGE,"E77");var subQ1=sQuery(id+"F9.wireOp",EDGE,"E63");var subQ2=makeQuery(id+"F9.imprint","INTERSECT",VERTEX,{"derivedFrom":[subQ1,subQ0]});Q26=makeQuery(id+"F9.imprint","IMPRINT",FACE,{"disambiguationData":[TD([[makeQuery(id+"F9.imprint","IMPRINT",EDGE,{"disambiguationData":[TD([[subQ2,-1.0]])],"derivedFrom":subQ1}),1.0]])]});}
            var Q27;
            {var subQ0=sQuery(id+"F9.wireOp",EDGE,"E109.trimOffspring");var subQ1=sQuery(id+"F9.wireOp",EDGE,"E63");var subQ2=makeQuery(id+"F9.imprint","INTERSECT",VERTEX,{"derivedFrom":[subQ1,subQ0]});Q27=makeQuery(id+"F9.imprint","IMPRINT",FACE,{"disambiguationData":[TD([[makeQuery(id+"F9.imprint","IMPRINT",EDGE,{"disambiguationData":[TD([[subQ2,-1.0]])],"derivedFrom":subQ1}),1.0]])]});}
            var Q28;
            {var subQ0=sQuery(id+"F9.wireOp",EDGE,"E109.trimOffspring");var subQ1=sQuery(id+"F9.wireOp",EDGE,"E63");var subQ2=makeQuery(id+"F9.imprint","INTERSECT",VERTEX,{"derivedFrom":[subQ1,subQ0]});Q28=makeQuery(id+"F9.imprint","IMPRINT",FACE,{"disambiguationData":[TD([[makeQuery(id+"F9.imprint","IMPRINT",EDGE,{"disambiguationData":[TD([[subQ2,-1.0]])],"derivedFrom":subQ1}),-1.0]])]});}
            var Q29;
            {var subQ0=sQuery(id+"F9.wireOp",EDGE,"E77");var subQ1=sQuery(id+"F9.wireOp",EDGE,"E63");var subQ2=makeQuery(id+"F9.imprint","INTERSECT",VERTEX,{"derivedFrom":[subQ1,subQ0]});Q29=makeQuery(id+"F9.imprint","IMPRINT",FACE,{"disambiguationData":[TD([[makeQuery(id+"F9.imprint","IMPRINT",EDGE,{"disambiguationData":[TD([[subQ2,-1.0]])],"derivedFrom":subQ1}),-1.0]])]});}
            var Q30;
            {var subQ0=sQuery(id+"F9.wireOp",EDGE,"E78");Q30=makeQuery(id+"F9.imprint","IMPRINT",FACE,{"disambiguationData":[TD([[makeQuery(id+"F9.imprint","IMPRINT",EDGE,{"derivedFrom":subQ0}),1.0]])]});}
            var Q31;
            {var subQ0=sQuery(id+"F9.wireOp",EDGE,"E78");Q31=makeQuery(id+"F9.imprint","IMPRINT",FACE,{"disambiguationData":[TD([[makeQuery(id+"F9.imprint","IMPRINT",EDGE,{"derivedFrom":subQ0}),-1.0]])]});}
            var Q32;
            {var subQ6=sQuery(id+"F9.wireOp",EDGE,"E61");Q32=makeQuery(id+"F9.imprint","IMPRINT",FACE,{"disambiguationData":[TD([[makeQuery(id+"F9.imprint","IMPRINT",EDGE,{"derivedFrom":subQ6}),1.0]])]});}
            var Q33;
            {var subQ0=sQuery(id+"F9.wireOp",EDGE,"E119.trimOffspring");var subQ1=sQuery(id+"F9.wireOp",EDGE,"E63");var subQ2=makeQuery(id+"F9.imprint","INTERSECT",VERTEX,{"derivedFrom":[subQ1,subQ0]});Q33=makeQuery(id+"F9.imprint","IMPRINT",FACE,{"disambiguationData":[TD([[makeQuery(id+"F9.imprint","IMPRINT",EDGE,{"disambiguationData":[TD([[subQ2,-1.0]])],"derivedFrom":subQ1}),-1.0]])]});}
            var Q34;
            {var subQ0=sQuery(id+"F9.wireOp",EDGE,"E73");var subQ1=sQuery(id+"F9.wireOp",EDGE,"E63");var subQ2=makeQuery(id+"F9.imprint","INTERSECT",VERTEX,{"derivedFrom":[subQ1,subQ0]});Q34=makeQuery(id+"F9.imprint","IMPRINT",FACE,{"disambiguationData":[TD([[makeQuery(id+"F9.imprint","IMPRINT",EDGE,{"disambiguationData":[TD([[subQ2,-1.0]])],"derivedFrom":subQ1}),-1.0]])]});}
            extrude(context, id + "F10", {"entities" : qUnion([Q0, Q1, Q2, Q3, Q4, Q5, Q6, Q7, Q8, Q9, Q10, Q11, Q12, Q13, Q14, Q15, Q16, Q17, Q18, Q19, Q20, Q21, Q22, Q23, Q24, Q25, Q26, Q27, Q28, Q29, Q30, Q31, Q32, Q33, Q34]), "operationType" : NewBodyOperationType.REMOVE, "oppositeDirection" : true, "depth" : 0.5 * mm});
        }
        {
            var Q0;
            Q0=makeQuery(id+"F10.boolean.opBoolean","MERGE",FACE,{"derivedFrom":[makeQuery(id+"F1.opExtrude","SWEPT_FACE",FACE,{"disambiguationData":[OSD([sQuery(id+"F0.wireOp",EDGE,"E3")])]}),makeQuery(id+"F10.opExtrude","SWEPT_FACE",FACE,{"disambiguationData":[OSD([sQuery(id+"F9.wireOp",EDGE,"E61")])]})]});
            var sketch = newSketch(context, id + "F11", { "sketchPlane" : qUnion([Q0])});
            skLineSegment(sketch, "E131.bottom", {"start": v(470, 10) * mm, "end": v(260, 10) * mm});
            skLineSegment(sketch, "E131.top", {"start": v(470, 15) * mm, "end": v(265, 15) * mm});
            skLineSegment(sketch, "E131.left", {"start": v(470, 10) * mm, "end": v(470, 15) * mm});
            skLineSegment(sketch, "E132", {"start": v(265, 15) * mm, "end": v(265, 55) * mm});
            skLineSegment(sketch, "E133", {"start": v(265, 55) * mm, "end": v(0, 55) * mm});
            skLineSegment(sketch, "E134", {"start": v(0, 55) * mm, "end": v(0, 50) * mm});
            skLineSegment(sketch, "E135", {"start": v(0, 50) * mm, "end": v(260, 50) * mm});
            skLineSegment(sketch, "E136", {"start": v(260, 50) * mm, "end": v(260, 10) * mm});
            skPoint(sketch, "E137.trimOffspring.end.orphan", {"position": v(0, 35) * mm});
            skSolve(sketch);
        }
        {
            var Q0;
            Q0=qSketchRegion(id+"F11",true);
            extrude(context, id + "F12", {"entities" : qUnion([Q0]), "oppositeDirection" : true, "depth" : 40 * mm});
        }
        {
            var Q0;
            Q0=makeQuery(id+"F12.opExtrude","SWEPT_FACE",FACE,{"disambiguationData":[OSD([sQuery(id+"F11.wireOp",EDGE,"E131.top")])]});
            var sketch = newSketch(context, id + "F13", { "sketchPlane" : qUnion([Q0])});
            skCircle(sketch, "E138", {"center": v(40, 450) * mm, "radius": 5 * mm});
            skPoint(sketch, "E138.centerSnap0", {"position": v(40, 470) * mm});
            skSolve(sketch);
        }
        {
            var Q0;
            Q0=qSketchRegion(id+"F13",true);
            extrude(context, id + "F14", {"entities" : qUnion([Q0]), "operationType" : NewBodyOperationType.REMOVE, "oppositeDirection" : true, "depth" : 10 * mm});
        }
        {
            var Q0;
            Q0=makeQuery(id+"F12.opExtrude","SWEPT_FACE",FACE,{"disambiguationData":[OSD([sQuery(id+"F11.wireOp",EDGE,"E131.top")])]});
            var sketch = newSketch(context, id + "F15", { "sketchPlane" : qUnion([Q0])});
            skLineSegment(sketch, "E139.bottom", {"start": v(30, 362.1) * mm, "end": v(50, 362.1) * mm});
            skLineSegment(sketch, "E139.top", {"start": v(30, 312.1) * mm, "end": v(50, 312.1) * mm});
            skLineSegment(sketch, "E139.left", {"start": v(30, 362.1) * mm, "end": v(30, 312.1) * mm});
            skLineSegment(sketch, "E139.right", {"start": v(50, 362.1) * mm, "end": v(50, 312.1) * mm});
            skPoint(sketch, "E139.middle", {"position": v(40, 337.1) * mm});
            skPoint(sketch, "E139.middle.positionSnap0", {"position": v(40, 470) * mm});
            skPoint(sketch, "E139.centerSnap0", {"position": v(40, 470) * mm});
            skLineSegment(sketch, "E140", {"start": v(30, 362.1) * mm, "end": v(40, 350.1) * mm});
            skLineSegment(sketch, "E141", {"start": v(40, 350.1) * mm, "end": v(50, 362.1) * mm});
            skLineSegment(sketch, "E142", {"start": v(30, 312.1) * mm, "end": v(40, 324.1) * mm});
            skPoint(sketch, "E142.endSnap0", {"position": v(40, 312.1) * mm});
            skLineSegment(sketch, "E143", {"start": v(40, 324.1) * mm, "end": v(50, 312.1) * mm});
            skSolve(sketch);
        }
        {
            var Q0;
            Q0=makeQuery(id+"F15.imprint","IMPRINT",FACE,{"disambiguationData":[TD([[makeQuery(id+"F15.imprint","IMPRINT",EDGE,{"derivedFrom":sQuery(id+"F15.wireOp",EDGE,"E139.left")}),1.0]])]});
            extrude(context, id + "F16", {"entities" : qUnion([Q0]), "operationType" : NewBodyOperationType.REMOVE, "oppositeDirection" : true, "depth" : 10 * mm});
        }
        {
            var Q0;
            Q0=makeQuery(id+"F12.opExtrude","SWEPT_FACE",FACE,{"disambiguationData":[OSD([sQuery(id+"F11.wireOp",EDGE,"E133")])]});
            var sketch = newSketch(context, id + "F17", { "sketchPlane" : qUnion([Q0])});
            skLineSegment(sketch, "E144.bottom", {"start": v(30, 75) * mm, "end": v(50, 75) * mm});
            skLineSegment(sketch, "E144.top", {"start": v(30, 25) * mm, "end": v(50, 25) * mm});
            skLineSegment(sketch, "E144.left", {"start": v(30, 75) * mm, "end": v(30, 25) * mm});
            skLineSegment(sketch, "E144.right", {"start": v(50, 75) * mm, "end": v(50, 25) * mm});
            skPoint(sketch, "E144.middle", {"position": v(40, 50) * mm});
            skPoint(sketch, "E144.middle.positionSnap0", {"position": v(40, 0) * mm});
            skPoint(sketch, "E144.centerSnap0", {"position": v(40, 0) * mm});
            skLineSegment(sketch, "E145", {"start": v(30, 75) * mm, "end": v(40, 69) * mm});
            skPoint(sketch, "E145.endSnap0", {"position": v(40, 25) * mm});
            skLineSegment(sketch, "E146", {"start": v(40, 69) * mm, "end": v(50, 75) * mm});
            skLineSegment(sketch, "E147", {"start": v(30, 25) * mm, "end": v(40, 31) * mm});
            skLineSegment(sketch, "E148", {"start": v(40, 31) * mm, "end": v(50, 25) * mm});
            skSolve(sketch);
        }
        {
            var Q0;
            Q0=makeQuery(id+"F17.imprint","IMPRINT",FACE,{"disambiguationData":[TD([[makeQuery(id+"F17.imprint","IMPRINT",EDGE,{"derivedFrom":sQuery(id+"F17.wireOp",EDGE,"E144.left")}),1.0]])]});
            extrude(context, id + "F18", {"entities" : qUnion([Q0]), "operationType" : NewBodyOperationType.REMOVE, "oppositeDirection" : true, "depth" : 10 * mm});
        }
        {
            var Q0;
            Q0=makeQuery(id+"F12.opExtrude","SWEPT_FACE",FACE,{"disambiguationData":[OSD([sQuery(id+"F11.wireOp",EDGE,"E131.top")])]});
            var sketch = newSketch(context, id + "F19", { "sketchPlane" : qUnion([Q0])});
            skLineSegment(sketch, "E149", {"start": v(40, 350.1) * mm, "end": v(40, 375.1) * mm});
            skLineSegment(sketch, "E150", {"start": v(40, 375.1) * mm, "end": v(40.25, 375.1) * mm});
            skLineSegment(sketch, "E151", {"start": v(40.25, 375.1) * mm, "end": v(40.25, 350.4) * mm});
            skLineSegment(sketch, "E152", {"start": v(40, 375.1) * mm, "end": v(39.75, 375.1) * mm});
            skLineSegment(sketch, "E153", {"start": v(39.75, 375.1) * mm, "end": v(39.75, 350.4) * mm});
            skLineSegment(sketch, "E154", {"start": v(39.75, 350.4) * mm, "end": v(40, 350.1) * mm});
            skLineSegment(sketch, "E155", {"start": v(40.25, 350.4) * mm, "end": v(40, 350.1) * mm});
            skLineSegment(sketch, "E156", {"start": v(40, 324.1) * mm, "end": v(40, 299.1) * mm});
            skLineSegment(sketch, "E157", {"start": v(40, 299.1) * mm, "end": v(40.25, 299.1) * mm});
            skLineSegment(sketch, "E158", {"start": v(40.25, 299.1) * mm, "end": v(40.25, 323.8) * mm});
            skLineSegment(sketch, "E159", {"start": v(40.25, 323.8) * mm, "end": v(40, 324.1) * mm});
            skLineSegment(sketch, "E160", {"start": v(40, 299.1) * mm, "end": v(39.75, 299.1) * mm});
            skLineSegment(sketch, "E161", {"start": v(39.75, 299.1) * mm, "end": v(39.75, 323.8) * mm});
            skLineSegment(sketch, "E162", {"start": v(39.75, 323.8) * mm, "end": v(40, 324.1) * mm});
            skSolve(sketch);
        }
        {
            var Q0;
            Q0=qSketchRegion(id+"F19",true);
            extrude(context, id + "F20", {"entities" : qUnion([Q0]), "operationType" : NewBodyOperationType.REMOVE, "oppositeDirection" : true, "depth" : 0.5 * mm});
        }
        {
            var Q0;
            Q0=makeQuery(id+"F12.opExtrude","SWEPT_FACE",FACE,{"disambiguationData":[OSD([sQuery(id+"F11.wireOp",EDGE,"E133")])]});
            var sketch = newSketch(context, id + "F21", { "sketchPlane" : qUnion([Q0])});
            skLineSegment(sketch, "E163", {"start": v(40, 69) * mm, "end": v(40, 79) * mm});
            skLineSegment(sketch, "E164", {"start": v(40, 79) * mm, "end": v(40.25, 79) * mm});
            skLineSegment(sketch, "E165", {"start": v(40.25, 79) * mm, "end": v(40.25, 69.15) * mm});
            skLineSegment(sketch, "E166", {"start": v(40.25, 69.15) * mm, "end": v(40, 69) * mm});
            skLineSegment(sketch, "E167", {"start": v(40, 79) * mm, "end": v(39.75, 79) * mm});
            skLineSegment(sketch, "E168", {"start": v(39.75, 79) * mm, "end": v(39.75, 69.15) * mm});
            skLineSegment(sketch, "E169", {"start": v(39.75, 69.15) * mm, "end": v(40, 69) * mm});
            skLineSegment(sketch, "E170", {"start": v(40, 31) * mm, "end": v(40, 21) * mm});
            skLineSegment(sketch, "E171", {"start": v(40, 21) * mm, "end": v(40.25, 21) * mm});
            skLineSegment(sketch, "E172", {"start": v(40.25, 21) * mm, "end": v(40.25, 30.85) * mm});
            skLineSegment(sketch, "E173", {"start": v(40.25, 30.85) * mm, "end": v(40, 31) * mm});
            skLineSegment(sketch, "E174", {"start": v(40, 21) * mm, "end": v(39.75, 21) * mm});
            skLineSegment(sketch, "E175", {"start": v(39.75, 21) * mm, "end": v(39.75, 30.85) * mm});
            skLineSegment(sketch, "E176", {"start": v(39.75, 30.85) * mm, "end": v(40, 31) * mm});
            skSolve(sketch);
        }
        {
            var Q0;
            Q0=qSketchRegion(id+"F21",true);
            extrude(context, id + "F22", {"entities" : qUnion([Q0]), "operationType" : NewBodyOperationType.REMOVE, "oppositeDirection" : true, "depth" : 0.25 * mm});
        }
        {
            var Q0;
            Q0=makeQuery(id+"F1.opExtrude","SWEPT_EDGE",EDGE,{"disambiguationData":[OSD([sQuery(id+"F0.wireOp",EDGE,"E33"),sQuery(id+"F0.wireOp",EDGE,"E34")])]});
            var Q1;
            Q1=makeQuery(id+"F1.opExtrude","SWEPT_EDGE",EDGE,{"disambiguationData":[OSD([sQuery(id+"F0.wireOp",EDGE,"E29"),sQuery(id+"F0.wireOp",EDGE,"E30")])]});
            fillet(context, id + "F23", {"entities" : qUnion([Q0, Q1]), "radius" : 50 * mm, "tangentPropagation" : true, "allowEdgeOverflow" : false});
        }
        {
            var Q0;
            Q0=makeQuery(id+"F1.opExtrude","SWEPT_EDGE",EDGE,{"disambiguationData":[OSD([sQuery(id+"F0.wireOp",EDGE,"E27"),sQuery(id+"F0.wireOp",EDGE,"E28")])]});
            var Q1;
            Q1=makeQuery(id+"F1.opExtrude","SWEPT_EDGE",EDGE,{"disambiguationData":[OSD([sQuery(id+"F0.wireOp",EDGE,"E32"),sQuery(id+"F0.wireOp",EDGE,"E33")])]});
            var Q2;
            Q2=makeQuery(id+"F1.opExtrude","SWEPT_EDGE",EDGE,{"disambiguationData":[OSD([sQuery(id+"F0.wireOp",EDGE,"E23"),sQuery(id+"F0.wireOp",EDGE,"E24")])]});
            fillet(context, id + "F24", {"entities" : qUnion([Q0, Q1, Q2]), "radius" : 20 * mm, "tangentPropagation" : true, "allowEdgeOverflow" : false});
        }
        {
            var Q0;
            Q0=makeQuery(id+"F12.opExtrude","CAP_EDGE",EDGE,{"disambiguationData":[OSD([sQuery(id+"F11.wireOp",EDGE,"E134")])],"isStart":true});
            var Q1;
            Q1=makeQuery(id+"F12.opExtrude","CAP_EDGE",EDGE,{"disambiguationData":[OSD([sQuery(id+"F11.wireOp",EDGE,"E134")])],"isStart":false});
            var Q2;
            Q2=makeQuery(id+"F12.opExtrude","CAP_EDGE",EDGE,{"disambiguationData":[OSD([sQuery(id+"F11.wireOp",EDGE,"E131.left")])],"isStart":false});
            var Q3;
            Q3=makeQuery(id+"F12.opExtrude","CAP_EDGE",EDGE,{"disambiguationData":[OSD([sQuery(id+"F11.wireOp",EDGE,"E131.left")])],"isStart":true});
            fillet(context, id + "F25", {"entities" : qUnion([Q0, Q1, Q2, Q3]), "radius" : 20 * mm, "tangentPropagation" : true, "allowEdgeOverflow" : false});
        }
        {
            var Q0;
            Q0=makeQuery(id+"F12.opExtrude","SWEPT_EDGE",EDGE,{"disambiguationData":[OSD([sQuery(id+"F11.wireOp",EDGE,"E132"),sQuery(id+"F11.wireOp",EDGE,"E133")])]});
            var Q1;
            Q1=makeQuery(id+"F12.opExtrude","SWEPT_EDGE",EDGE,{"disambiguationData":[OSD([sQuery(id+"F11.wireOp",EDGE,"E131.bottom"),sQuery(id+"F11.wireOp",EDGE,"E136")])]});
            fillet(context, id + "F26", {"entities" : qUnion([Q0, Q1]), "radius" : 10 * mm, "tangentPropagation" : true, "allowEdgeOverflow" : false});
        }
        {
            var Q0;
            Q0=makeQuery(id+"F12.opExtrude","SWEPT_EDGE",EDGE,{"disambiguationData":[OSD([sQuery(id+"F11.wireOp",EDGE,"E131.top"),sQuery(id+"F11.wireOp",EDGE,"E132")])]});
            var Q1;
            Q1=makeQuery(id+"F12.opExtrude","SWEPT_EDGE",EDGE,{"disambiguationData":[OSD([sQuery(id+"F11.wireOp",EDGE,"E135"),sQuery(id+"F11.wireOp",EDGE,"E136")])]});
            fillet(context, id + "F27", {"entities" : qUnion([Q0, Q1]), "radius" : 5 * mm, "tangentPropagation" : true, "allowEdgeOverflow" : false});
        }
        {
            var Q0;
            Q0=qCreatedBy(makeId("Right.planeOp"),FACE);
            var sketch = newSketch(context, id + "F28", { "sketchPlane" : qUnion([Q0])});
            skArc(sketch, "E177", {"start": v(-47.48, 41.9) * mm, "mid": v(-68.98, 63.4) * mm, "end": v(-90.48, 41.9) * mm});
            skLineSegment(sketch, "E178", {"start": v(-47.48, 41.9) * mm, "end": v(-47.48, 20.4) * mm});
            skLineSegment(sketch, "E179", {"start": v(-90.48, 41.9) * mm, "end": v(-90.48, 20.4) * mm});
            skSolve(sketch);
        }
        {
            var Q0;
            Q0=sQuery(id+"F28.wireOp",VERTEX,"E179.end");
            var Q1;
            Q1=qCreatedBy(makeId("Top.planeOp"),FACE);
            cPlane(context, id + "F29", {"entities" : qUnion([Q0, Q1]), "cplaneType" : CPlaneType.PLANE_POINT, "offset" : 25 * mm, "width" : 150 * mm, "height" : 150 * mm});
        }
        {
            var Q0;
            Q0=qCreatedBy(id+"F29.planeOp",FACE);
            var sketch = newSketch(context, id + "F30", { "sketchPlane" : qUnion([Q0])});
            skCircle(sketch, "E180", {"center": v(0, -90.48) * mm, "radius": 5 * mm});
            skSolve(sketch);
        }
        {
            var Q0;
            Q0=makeQuery(id+"F30.imprint","IMPRINT",FACE,{"disambiguationData":[TD([[makeQuery(id+"F30.imprint","IMPRINT",EDGE,{"derivedFrom":sQuery(id+"F30.wireOp",EDGE,"E180")}),1.0]])]});
            var Q1;
            Q1=sQuery(id+"F28.wireOp",EDGE,"E179");
            var Q2;
            Q2=sQuery(id+"F28.wireOp",EDGE,"E177");
            var Q3;
            Q3=sQuery(id+"F28.wireOp",EDGE,"E178");
            sweep(context, id + "F31", {"profiles" : qUnion([Q0]), "path" : qUnion([Q1, Q2, Q3])});
        }
        {
            var Q0;
            Q0=qCreatedBy(makeId("Right.planeOp"),FACE);
            var sketch = newSketch(context, id + "F32", { "sketchPlane" : qUnion([Q0])});
            skLineSegment(sketch, "E181", {"start": v(-114.2, 20.99) * mm, "end": v(-139.2, 20.99) * mm});
            skArc(sketch, "E182", {"start": v(-139.2, 40.56) * mm, "mid": v(-158.2, 59.56) * mm, "end": v(-177.2, 40.56) * mm});
            skArc(sketch, "E183.0", {"start": v(-134.2, 40.56) * mm, "mid": v(-158.2, 64.56) * mm, "end": v(-182.2, 40.56) * mm});
            skLineSegment(sketch, "E184.left", {"start": v(-139.2, 40.56) * mm, "end": v(-139.2, 20.99) * mm});
            skLineSegment(sketch, "E184.right", {"start": v(-134.2, 40.56) * mm, "end": v(-134.2, 26.56) * mm});
            skLineSegment(sketch, "E185.left", {"start": v(-177.2, 40.56) * mm, "end": v(-177.2, 20.99) * mm});
            skLineSegment(sketch, "E185.right", {"start": v(-182.2, 40.56) * mm, "end": v(-182.2, 26.56) * mm});
            skLineSegment(sketch, "E186", {"start": v(-134.2, 26.56) * mm, "end": v(-114.2, 26.56) * mm});
            skLineSegment(sketch, "E187", {"start": v(-114.2, 26.56) * mm, "end": v(-114.2, 20.99) * mm});
            skLineSegment(sketch, "E188", {"start": v(-182.2, 26.56) * mm, "end": v(-202.2, 26.56) * mm});
            skLineSegment(sketch, "E189", {"start": v(-202.2, 26.56) * mm, "end": v(-202.2, 20.99) * mm});
            skPoint(sketch, "E190.orphan", {"position": v(-139.2, 16.56) * mm});
            skLineSegment(sketch, "E191.trimOffspring", {"start": v(-177.2, 20.99) * mm, "end": v(-220.09, 20.99) * mm});
            skPoint(sketch, "E192.trimOffspring.end.orphan", {"position": v(-182.2, 16.56) * mm});
            skSolve(sketch);
        }
        {
            var Q0;
            Q0=qSketchRegion(id+"F32",true);
            extrude(context, id + "F33", {"entities" : qUnion([Q0]), "depth" : 25 * mm});
        }
        {
            var Q0;
            Q0=makeQuery(id+"F1.opExtrude","CAP_FACE",FACE,{"disambiguationData":[OSD([sQuery(id+"F0.wireOp",EDGE,"E3"),sQuery(id+"F0.wireOp",EDGE,"E4"),sQuery(id+"F0.wireOp",EDGE,"E14"),sQuery(id+"F0.wireOp",EDGE,"E20"),sQuery(id+"F0.wireOp",EDGE,"E23"),sQuery(id+"F0.wireOp",EDGE,"E24"),sQuery(id+"F0.wireOp",EDGE,"E27"),sQuery(id+"F0.wireOp",EDGE,"E28"),sQuery(id+"F0.wireOp",EDGE,"E29"),sQuery(id+"F0.wireOp",EDGE,"E30"),sQuery(id+"F0.wireOp",EDGE,"E32"),sQuery(id+"F0.wireOp",EDGE,"E33"),sQuery(id+"F0.wireOp",EDGE,"E34")])],"isStart":false});
            var sketch = newSketch(context, id + "F34", { "sketchPlane" : qUnion([Q0])});
            skCircle(sketch, "E193", {"center": v(430.85, 419) * mm, "radius": 10 * mm});
            skCircle(sketch, "E194", {"center": v(488.87, 419) * mm, "radius": 10 * mm});
            skCircle(sketch, "E195", {"center": v(403.77, 289.52) * mm, "radius": 10 * mm});
            skCircle(sketch, "E196", {"center": v(457.8, 268.42) * mm, "radius": 10 * mm});
            skArc(sketch, "E197", {"start": v(467.07, 264.68) * mm, "mid": v(489.93, 340.29) * mm, "end": v(498.86, 418.77) * mm});
            skArc(sketch, "E198.0", {"start": v(448.52, 272.17) * mm, "mid": v(470.34, 344.33) * mm, "end": v(478.87, 419.23) * mm});
            skArc(sketch, "E199.0", {"start": v(413.03, 285.76) * mm, "mid": v(432.91, 351) * mm, "end": v(440.84, 418.73) * mm});
            skArc(sketch, "E200.0", {"start": v(394.5, 293.28) * mm, "mid": v(413.34, 355.1) * mm, "end": v(420.85, 419.27) * mm});
            skSolve(sketch);
        }
        {
            var Q0;
            Q0 = qSketchRegion(id + "F34", true);
            extrude(context, id + "F35", {"entities" : qUnion([Q0]), "operationType" : NewBodyOperationType.REMOVE, "oppositeDirection" : true, "depth" : 3 * mm});
        }
    });
